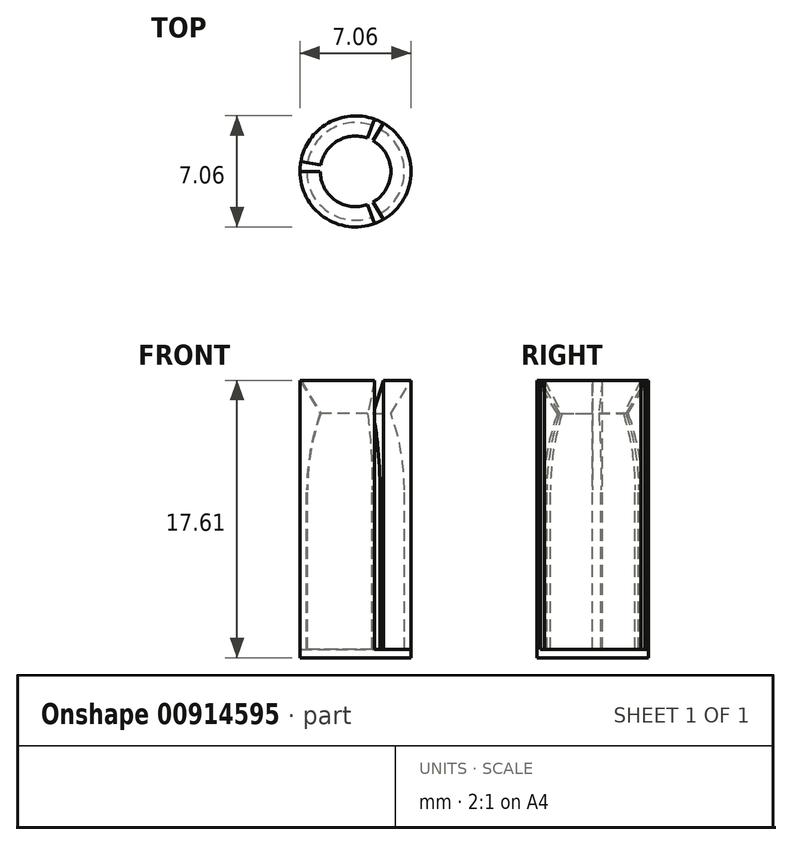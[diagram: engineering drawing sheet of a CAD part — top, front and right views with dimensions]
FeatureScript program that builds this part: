
annotation { "Feature Type Name" : "Feature", "Feature Type Description" : "" }
export const myFeature = defineFeature(function(context is Context, id is Id, definition is map)
    precondition{}
    {
        {
            var Q0;
            Q0=qCreatedBy(makeId("Front.planeOp"),FACE);
            var sketch = newSketch(context, id + "F0", { "sketchPlane" : qUnion([Q0])});
            skLineSegment(sketch, "E0", {"start": v(-3.28, -0.53) * mm, "end": v(0, -0.53) * mm});
            skLineSegment(sketch, "E1", {"start": v(0, -0.53) * mm, "end": v(0, 0) * mm});
            skLineSegment(sketch, "E2", {"start": v(-3.1, 0) * mm, "end": v(0, 0) * mm});
            skLineSegment(sketch, "E3", {"start": v(-3.1, 0) * mm, "end": v(-3.1, 10.12) * mm});
            skLineSegment(sketch, "E4", {"start": v(-3.28, 16.68) * mm, "end": v(-2.24, 14.98) * mm});
            skArc(sketch, "E5", {"start": v(-2.24, 14.98) * mm, "mid": v(-2.88, 12.59) * mm, "end": v(-3.1, 10.12) * mm});
            skLineSegment(sketch, "E6", {"start": v(-2.24, 14.98) * mm, "end": v(-3.53, 17.08) * mm});
            skLineSegment(sketch, "E7", {"start": v(0, -0.53) * mm, "end": v(-3.53, -0.53) * mm});
            skLineSegment(sketch, "E8", {"start": v(-3.53, -0.53) * mm, "end": v(-3.53, 17.08) * mm});
            skLineSegment(sketch, "E9", {"start": v(-3.53, 0) * mm, "end": v(0, 0) * mm});
            skSolve(sketch);
        }
        {
            var Q0;
            {var subQ0=sQuery(id+"F0.wireOp",EDGE,"E3");Q0=makeQuery(id+"F0.imprint","IMPRINT",FACE,{"disambiguationData":[TD([[makeQuery(id+"F0.imprint","IMPRINT",EDGE,{"derivedFrom":subQ0}),1.0]])]});}
            var Q1;
            Q1=sQuery(id+"F0.wireOp",EDGE,"E1");
            revolve(context, id + "F1", {"surfaceOperationType" : NewSurfaceOperationType.NEW, "entities" : qUnion([Q0]), "axis" : qUnion([Q1]), "revolveType" : RevolveType.ONE_DIRECTION, "oppositeDirection" : true, "angle" : 10 * degree});
        }
        {
            var Q0;
            Q0=makeQuery(id+"F1.opRevolve","CAP_FACE",FACE,{"disambiguationData":[OSD([sQuery(id+"F0.wireOp",EDGE,"siq1ctb7-0nef-nmR8-9w7K-1SSss33n0AJs"),sQuery(id+"F0.wireOp",EDGE,"E3"),sQuery(id+"F0.wireOp",EDGE,"E4"),sQuery(id+"F0.wireOp",EDGE,"E5"),sQuery(id+"F0.wireOp",EDGE,"boG6fe4w-B7r5-aHth-cQcp-uLbW8xYjmA2T")])],"isStart":false});
            var Q1;
            Q1=sQuery(id+"F0.wireOp",EDGE,"E1");
            revolve(context, id + "F2", {"surfaceOperationType" : NewSurfaceOperationType.NEW, "entities" : qUnion([Q0]), "axis" : qUnion([Q1]), "revolveType" : RevolveType.ONE_DIRECTION, "oppositeDirection" : true, "angle" : 110 * degree});
        }
        {
            var Q0;
            Q0=makeQuery(id+"F2.opRevolve","CAP_FACE",FACE,{"disambiguationData":[OSD([sQuery(id+"F0.wireOp",EDGE,"siq1ctb7-0nef-nmR8-9w7K-1SSss33n0AJs"),sQuery(id+"F0.wireOp",EDGE,"E3"),sQuery(id+"F0.wireOp",EDGE,"E4"),sQuery(id+"F0.wireOp",EDGE,"E5"),sQuery(id+"F0.wireOp",EDGE,"boG6fe4w-B7r5-aHth-cQcp-uLbW8xYjmA2T")])],"isStart":false});
            var Q1;
            Q1=sQuery(id+"F0.wireOp",EDGE,"E1");
            revolve(context, id + "F3", {"surfaceOperationType" : NewSurfaceOperationType.NEW, "entities" : qUnion([Q0]), "axis" : qUnion([Q1]), "revolveType" : RevolveType.ONE_DIRECTION, "angle" : 10 * degree});
        }
        {
            var Q0;
            Q0=makeQuery(id+"F2.opRevolve","CAP_FACE",FACE,{"disambiguationData":[OSD([sQuery(id+"F0.wireOp",EDGE,"siq1ctb7-0nef-nmR8-9w7K-1SSss33n0AJs"),sQuery(id+"F0.wireOp",EDGE,"E3"),sQuery(id+"F0.wireOp",EDGE,"E4"),sQuery(id+"F0.wireOp",EDGE,"E5"),sQuery(id+"F0.wireOp",EDGE,"boG6fe4w-B7r5-aHth-cQcp-uLbW8xYjmA2T")])],"isStart":false});
            var Q1;
            Q1=sQuery(id+"F0.wireOp",EDGE,"E1");
            revolve(context, id + "F4", {"surfaceOperationType" : NewSurfaceOperationType.NEW, "entities" : qUnion([Q0]), "axis" : qUnion([Q1]), "revolveType" : RevolveType.ONE_DIRECTION, "oppositeDirection" : true, "angle" : 120 * degree});
        }
        {
            var Q0;
            Q0=makeQuery(id+"F2.opRevolve","CAP_FACE",FACE,{"disambiguationData":[OSD([sQuery(id+"F0.wireOp",EDGE,"siq1ctb7-0nef-nmR8-9w7K-1SSss33n0AJs"),sQuery(id+"F0.wireOp",EDGE,"E3"),sQuery(id+"F0.wireOp",EDGE,"E4"),sQuery(id+"F0.wireOp",EDGE,"E5"),sQuery(id+"F0.wireOp",EDGE,"boG6fe4w-B7r5-aHth-cQcp-uLbW8xYjmA2T")])],"isStart":true});
            var Q1;
            Q1=sQuery(id+"F0.wireOp",EDGE,"E1");
            revolve(context, id + "F5", {"operationType" : NewBodyOperationType.REMOVE, "surfaceOperationType" : NewSurfaceOperationType.NEW, "entities" : qUnion([Q0]), "axis" : qUnion([Q1]), "revolveType" : RevolveType.ONE_DIRECTION, "angle" : 10 * degree});
        }
        {
            var Q0;
            Q0=makeQuery(id+"F4.opRevolve","CAP_FACE",FACE,{"disambiguationData":[OSD([sQuery(id+"F0.wireOp",EDGE,"siq1ctb7-0nef-nmR8-9w7K-1SSss33n0AJs"),sQuery(id+"F0.wireOp",EDGE,"E3"),sQuery(id+"F0.wireOp",EDGE,"E4"),sQuery(id+"F0.wireOp",EDGE,"E5"),sQuery(id+"F0.wireOp",EDGE,"boG6fe4w-B7r5-aHth-cQcp-uLbW8xYjmA2T")])],"isStart":true});
            var Q1;
            Q1=sQuery(id+"F0.wireOp",EDGE,"E1");
            revolve(context, id + "F6", {"operationType" : NewBodyOperationType.REMOVE, "surfaceOperationType" : NewSurfaceOperationType.NEW, "entities" : qUnion([Q0]), "axis" : qUnion([Q1]), "revolveType" : RevolveType.ONE_DIRECTION, "angle" : 10 * degree});
        }
        {
            var Q0;
            {var subQ3=sQuery(id+"F0.wireOp",EDGE,"E0");Q0=makeQuery(id+"F0.imprint","IMPRINT",FACE,{"disambiguationData":[TD([[makeQuery(id+"F0.imprint","IMPRINT",EDGE,{"derivedFrom":subQ3}),1.0]])]});}
            var Q1;
            {var subQ5=sQuery(id+"F0.wireOp",EDGE,"E1");Q1=makeQuery(id+"F0.imprint","IMPRINT",FACE,{"disambiguationData":[TD([[makeQuery(id+"F0.imprint","IMPRINT",EDGE,{"derivedFrom":subQ5}),1.0]])]});}
            var Q2;
            Q2=sQuery(id+"F0.wireOp",EDGE,"E1");
            revolve(context, id + "F7", {"surfaceOperationType" : NewSurfaceOperationType.NEW, "entities" : qUnion([Q0, Q1]), "axis" : qUnion([Q2]), "revolveType" : RevolveType.FULL});
        }
        {
            var Q0;
            {var subQ6=sQuery(id+"F0.wireOp",EDGE,"E3");Q0=makeQuery(id+"F0.imprint","IMPRINT",FACE,{"disambiguationData":[TD([[makeQuery(id+"F0.imprint","IMPRINT",EDGE,{"derivedFrom":subQ6}),1.0]])]});}
            var Q1;
            Q1=sQuery(id+"F0.wireOp",EDGE,"E1");
            revolve(context, id + "F8", {"operationType" : NewBodyOperationType.ADD, "surfaceOperationType" : NewSurfaceOperationType.NEW, "entities" : qUnion([Q0]), "axis" : qUnion([Q1]), "revolveType" : RevolveType.ONE_DIRECTION, "angle" : 110 * degree});
        }
    });
